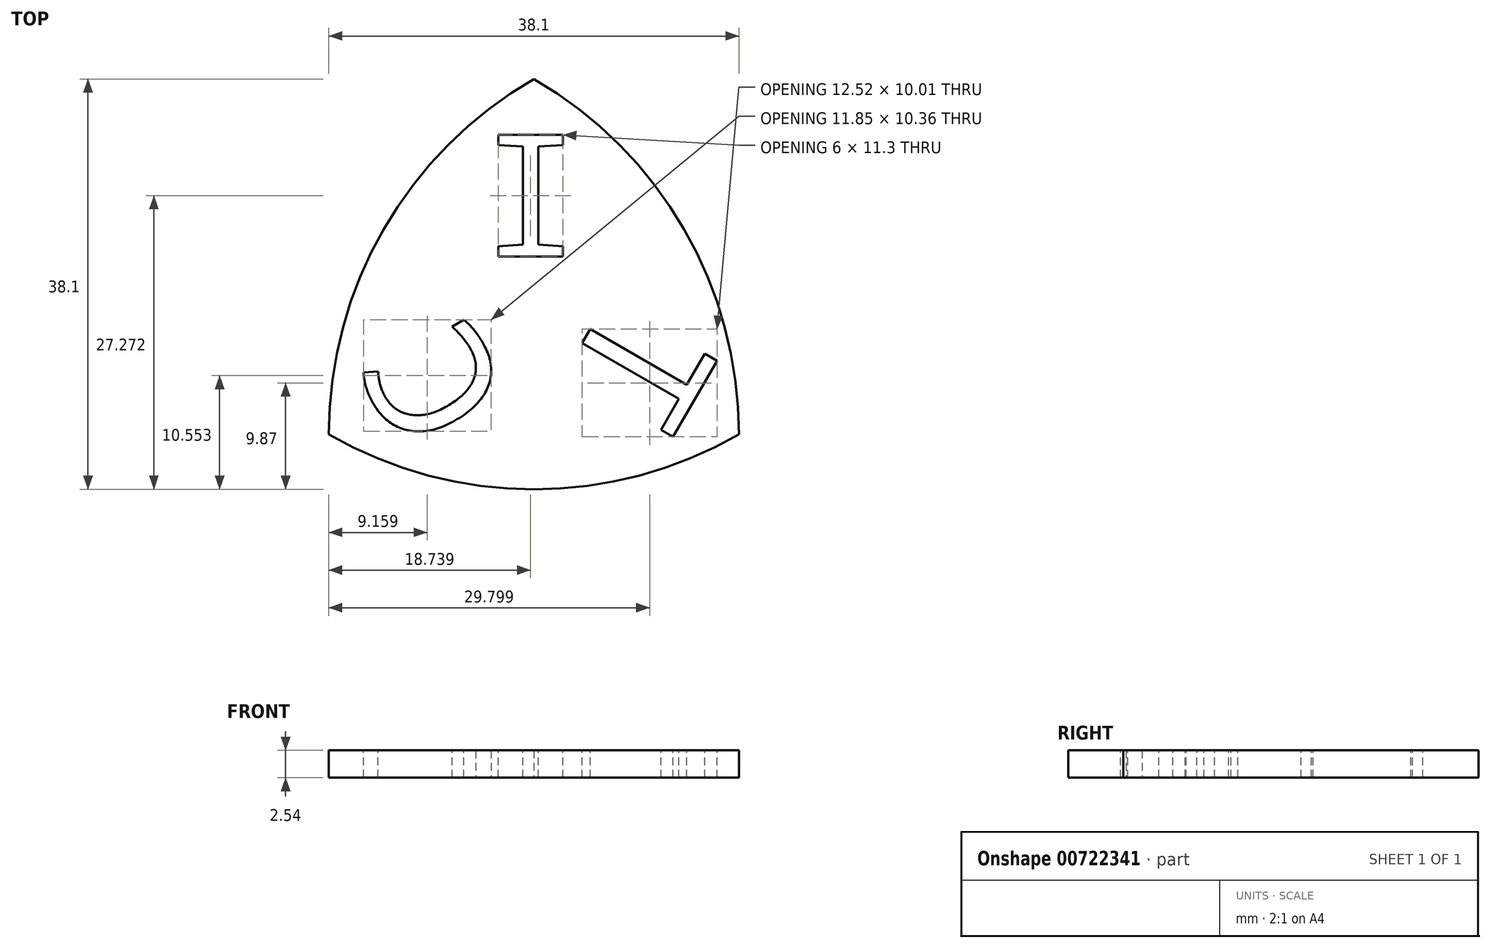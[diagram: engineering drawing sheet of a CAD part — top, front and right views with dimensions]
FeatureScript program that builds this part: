
annotation { "Feature Type Name" : "Feature", "Feature Type Description" : "" }
export const myFeature = defineFeature(function(context is Context, id is Id, definition is map)
    precondition{}
    {
        {
            var Q0;
            Q0=qCreatedBy(makeId("Top.planeOp"),FACE);
            var sketch = newSketch(context, id + "F0", { "sketchPlane" : qUnion([Q0])});
            skCircle(sketch, "E0", {"center": v(0, 0) * mm, "radius": 38.1 * mm});
            skSolve(sketch);
        }
        {
            var Q0;
            Q0=qCreatedBy(makeId("Top.planeOp"),FACE);
            var sketch = newSketch(context, id + "F1", { "sketchPlane" : qUnion([Q0])});
            skCircle(sketch, "E1", {"center": v(-38.1, 0) * mm, "radius": 38.1 * mm});
            skSolve(sketch);
        }
        {
            var Q0;
            Q0=qCreatedBy(makeId("Top.planeOp"),FACE);
            var sketch = newSketch(context, id + "F2", { "sketchPlane" : qUnion([Q0])});
            skCircle(sketch, "E2", {"center": v(-19.05, 33) * mm, "radius": 38.1 * mm});
            skSolve(sketch);
        }
        {
            var Q0;
            Q0=makeQuery(id+"F0.imprint","IMPRINT",FACE,{"disambiguationData":[TD([[makeQuery(id+"F0.imprint","IMPRINT",EDGE,{"derivedFrom":sQuery(id+"F0.wireOp",EDGE,"E0")}),1.0]])]});
            extrude(context, id + "F3", {"entities" : qUnion([Q0]), "depth" : 2.54 * mm, "offsetDistance" : 25.4 * mm});
        }
        {
            var Q0;
            Q0=makeQuery(id+"F1.imprint","IMPRINT",FACE,{"disambiguationData":[TD([[makeQuery(id+"F1.imprint","IMPRINT",EDGE,{"derivedFrom":sQuery(id+"F1.wireOp",EDGE,"E1")}),1.0]])]});
            extrude(context, id + "F4", {"entities" : qUnion([Q0]), "depth" : 2.54 * mm, "offsetDistance" : 25.4 * mm});
        }
        {
            var Q0;
            Q0=makeQuery(id+"F2.imprint","IMPRINT",FACE,{"disambiguationData":[TD([[makeQuery(id+"F2.imprint","IMPRINT",EDGE,{"derivedFrom":sQuery(id+"F2.wireOp",EDGE,"E2")}),1.0]])]});
            extrude(context, id + "F5", {"entities" : qUnion([Q0]), "depth" : 2.54 * mm, "offsetDistance" : 25.4 * mm});
        }
        {
            var Q0;
            Q0=makeQuery(id+"F3.opExtrude","SWEPT_BODY",BODY,{"disambiguationData":[OSD([sQuery(id+"F0.wireOp",EDGE,"E0")])]});
            var Q1;
            Q1=makeQuery(id+"F4.opExtrude","SWEPT_BODY",BODY,{"disambiguationData":[OSD([sQuery(id+"F1.wireOp",EDGE,"E1")])]});
            var Q2;
            Q2=makeQuery(id+"F5.opExtrude","SWEPT_BODY",BODY,{"disambiguationData":[OSD([sQuery(id+"F2.wireOp",EDGE,"E2")])]});
            booleanBodies(context, id + "F6", {"operationType" : BooleanOperationType.INTERSECTION, "tools" : qUnion([Q0, Q1, Q2])});
        }
        {
            var Q0;
            Q0=makeQuery(id+"F3.opExtrude","CAP_FACE",FACE,{"disambiguationData":[OSD([sQuery(id+"F0.wireOp",EDGE,"E0")])],"isStart":false});
            var sketch = newSketch(context, id + "F7", { "sketchPlane" : qUnion([Q0])});
            skText(sketch, "E3", { "text": "C", "fontName": "DroidSansMono.ttf"});
            skText(sketch, "E4", { "text": "I", "fontName": "DroidSansMono.ttf"});
            skText(sketch, "E5", { "text": "T", "fontName": "DroidSansMono.ttf"});
            const initialGuessF7  = {"E3": [-0.02095, 0.00326, -0.5, 0.86603, 0.0114], "E4": [-0.0241, 0.01652, 1, 0, 0.0114], "E5": [-0.01174, 0.01337, -0.5, -0.86603, 0.01177]};
            skSetInitialGuess(sketch, initialGuessF7);
            skSolve(sketch);
        }
        {
            var Q0;
            Q0 = qSketchRegion(id + "F7", true);
            extrude(context, id + "F8", {"entities" : qUnion([Q0]), "depth" : -2.54 * mm, "offsetDistance" : 25.4 * mm});
        }
        {
            var Q0;
            Q0=makeQuery(id+"F8.opExtrude","SWEPT_BODY",BODY,{"disambiguationData":[OSD([sQuery(id+"F7.wireOp",EDGE,"E4.sketch_text.stroke-0"),sQuery(id+"F7.wireOp",EDGE,"E4.sketch_text.stroke-1"),sQuery(id+"F7.wireOp",EDGE,"E4.sketch_text.stroke-2"),sQuery(id+"F7.wireOp",EDGE,"E4.sketch_text.stroke-3"),sQuery(id+"F7.wireOp",EDGE,"E4.sketch_text.stroke-4"),sQuery(id+"F7.wireOp",EDGE,"E4.sketch_text.stroke-5"),sQuery(id+"F7.wireOp",EDGE,"E4.sketch_text.stroke-6"),sQuery(id+"F7.wireOp",EDGE,"E4.sketch_text.stroke-7"),sQuery(id+"F7.wireOp",EDGE,"E4.sketch_text.stroke-8"),sQuery(id+"F7.wireOp",EDGE,"E4.sketch_text.stroke-9"),sQuery(id+"F7.wireOp",EDGE,"E4.sketch_text.stroke-10"),sQuery(id+"F7.wireOp",EDGE,"E4.sketch_text.stroke-11")])]});
            var Q1;
            Q1=makeQuery(id+"F8.opExtrude","SWEPT_BODY",BODY,{"disambiguationData":[OSD([sQuery(id+"F7.wireOp",EDGE,"E3.sketch_text.stroke-0"),sQuery(id+"F7.wireOp",EDGE,"E3.sketch_text.stroke-1"),sQuery(id+"F7.wireOp",EDGE,"E3.sketch_text.stroke-2"),sQuery(id+"F7.wireOp",EDGE,"E3.sketch_text.stroke-3"),sQuery(id+"F7.wireOp",EDGE,"E3.sketch_text.stroke-4"),sQuery(id+"F7.wireOp",EDGE,"E3.sketch_text.stroke-5"),sQuery(id+"F7.wireOp",EDGE,"E3.sketch_text.stroke-6"),sQuery(id+"F7.wireOp",EDGE,"E3.sketch_text.stroke-7"),sQuery(id+"F7.wireOp",EDGE,"E3.sketch_text.stroke-8"),sQuery(id+"F7.wireOp",EDGE,"E3.sketch_text.stroke-9"),sQuery(id+"F7.wireOp",EDGE,"E3.sketch_text.stroke-10"),sQuery(id+"F7.wireOp",EDGE,"E3.sketch_text.stroke-11"),sQuery(id+"F7.wireOp",EDGE,"E3.sketch_text.stroke-12"),sQuery(id+"F7.wireOp",EDGE,"E3.sketch_text.stroke-13")])]});
            var Q2;
            Q2=makeQuery(id+"F8.opExtrude","SWEPT_BODY",BODY,{"disambiguationData":[OSD([sQuery(id+"F7.wireOp",EDGE,"E5.sketch_text.stroke-0"),sQuery(id+"F7.wireOp",EDGE,"E5.sketch_text.stroke-1"),sQuery(id+"F7.wireOp",EDGE,"E5.sketch_text.stroke-2"),sQuery(id+"F7.wireOp",EDGE,"E5.sketch_text.stroke-3"),sQuery(id+"F7.wireOp",EDGE,"E5.sketch_text.stroke-4"),sQuery(id+"F7.wireOp",EDGE,"E5.sketch_text.stroke-5"),sQuery(id+"F7.wireOp",EDGE,"E5.sketch_text.stroke-6"),sQuery(id+"F7.wireOp",EDGE,"E5.sketch_text.stroke-7")])]});
            var Q3;
            Q3=makeQuery(id+"F6.opBoolean","INTERSECT",BODY,{"derivedFrom":[makeQuery(id+"F3.opExtrude","SWEPT_BODY",BODY,{"disambiguationData":[OSD([sQuery(id+"F0.wireOp",EDGE,"E0")])]}),makeQuery(id+"F4.opExtrude","SWEPT_BODY",BODY,{"disambiguationData":[OSD([sQuery(id+"F1.wireOp",EDGE,"E1")])]}),makeQuery(id+"F5.opExtrude","SWEPT_BODY",BODY,{"disambiguationData":[OSD([sQuery(id+"F2.wireOp",EDGE,"E2")])]})]});
            booleanBodies(context, id + "F9", {"operationType" : BooleanOperationType.SUBTRACTION, "tools" : qUnion([Q0, Q1, Q2]), "targets" : qUnion([Q3])});
        }
    });
